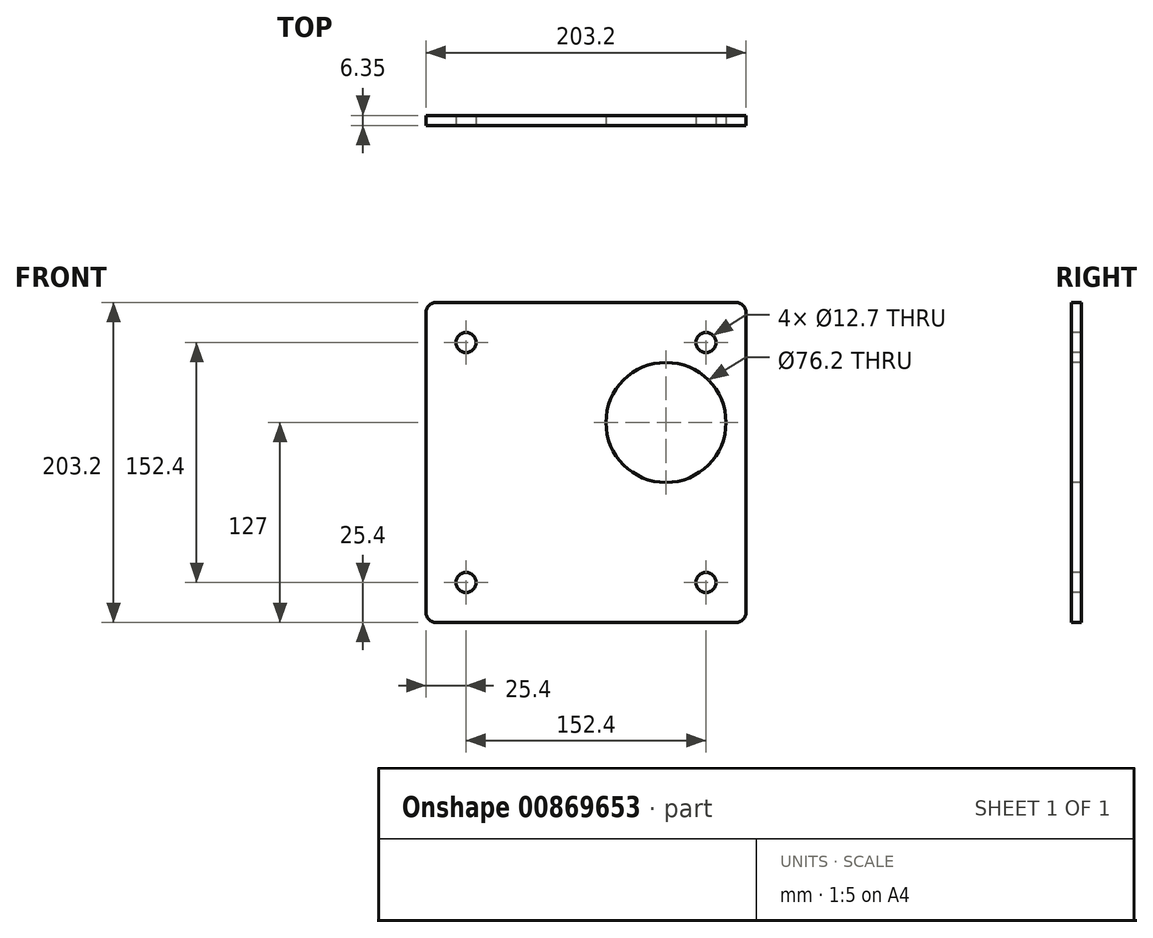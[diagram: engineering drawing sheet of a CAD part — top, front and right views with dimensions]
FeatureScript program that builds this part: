
annotation { "Feature Type Name" : "Feature", "Feature Type Description" : "" }
export const myFeature = defineFeature(function(context is Context, id is Id, definition is map)
    precondition{}
    {
        {
            var Q0;
            Q0=qCreatedBy(makeId("Front.planeOp"),FACE);
            var sketch = newSketch(context, id + "F0", { "sketchPlane" : qUnion([Q0])});
            skLineSegment(sketch, "E0.bottom", {"start": v(101.6, 101.6) * mm, "end": v(-101.6, 101.6) * mm});
            skLineSegment(sketch, "E0.top", {"start": v(101.6, -101.6) * mm, "end": v(-101.6, -101.6) * mm});
            skLineSegment(sketch, "E0.left", {"start": v(101.6, 101.6) * mm, "end": v(101.6, -101.6) * mm});
            skLineSegment(sketch, "E0.right", {"start": v(-101.6, 101.6) * mm, "end": v(-101.6, -101.6) * mm});
            skPoint(sketch, "E0.middle", {"position": v(0, 0) * mm});
            skSolve(sketch);
        }
        {
            var Q0;
            Q0=makeQuery(id+"F0.imprint","IMPRINT",FACE,{"disambiguationData":[TD([[makeQuery(id+"F0.imprint","IMPRINT",EDGE,{"derivedFrom":sQuery(id+"F0.wireOp",EDGE,"E0.bottom")}),1.0]])]});
            extrude(context, id + "F1", {"entities" : qUnion([Q0]), "depth" : 6.35 * mm, "offsetDistance" : 25.4 * mm});
        }
        {
            var Q0;
            Q0=makeQuery(id+"F1.opExtrude","CAP_FACE",FACE,{"disambiguationData":[OSD([sQuery(id+"F0.wireOp",EDGE,"E0.bottom"),sQuery(id+"F0.wireOp",EDGE,"E0.top"),sQuery(id+"F0.wireOp",EDGE,"E0.left"),sQuery(id+"F0.wireOp",EDGE,"E0.right")])],"isStart":false});
            var sketch = newSketch(context, id + "F2", { "sketchPlane" : qUnion([Q0])});
            skCircle(sketch, "E1", {"center": v(-76.2, 76.2) * mm, "radius": 6.35 * mm});
            skCircle(sketch, "E2", {"center": v(76.2, 76.2) * mm, "radius": 6.35 * mm});
            skCircle(sketch, "E3", {"center": v(-76.2, -76.2) * mm, "radius": 6.35 * mm});
            skCircle(sketch, "E4", {"center": v(76.2, -76.2) * mm, "radius": 6.35 * mm});
            skSolve(sketch);
        }
        {
            var Q0;
            Q0 = qSketchRegion(id + "F2", true);
            extrude(context, id + "F3", {"entities" : qUnion([Q0]), "operationType" : NewBodyOperationType.REMOVE, "oppositeDirection" : true, "depth" : 25.4 * mm, "offsetDistance" : 25.4 * mm});
        }
        {
            var Q0;
            Q0=makeQuery(id+"F1.opExtrude","SWEPT_EDGE",EDGE,{"disambiguationData":[OSD([sQuery(id+"F0.wireOp",EDGE,"E0.bottom"),sQuery(id+"F0.wireOp",EDGE,"E0.left")])]});
            var Q1;
            Q1=makeQuery(id+"F1.opExtrude","SWEPT_EDGE",EDGE,{"disambiguationData":[OSD([sQuery(id+"F0.wireOp",EDGE,"E0.bottom"),sQuery(id+"F0.wireOp",EDGE,"E0.right")])]});
            var Q2;
            Q2=makeQuery(id+"F1.opExtrude","SWEPT_EDGE",EDGE,{"disambiguationData":[OSD([sQuery(id+"F0.wireOp",EDGE,"E0.top"),sQuery(id+"F0.wireOp",EDGE,"E0.right")])]});
            var Q3;
            Q3=makeQuery(id+"F1.opExtrude","SWEPT_EDGE",EDGE,{"disambiguationData":[OSD([sQuery(id+"F0.wireOp",EDGE,"E0.top"),sQuery(id+"F0.wireOp",EDGE,"E0.left")])]});
            fillet(context, id + "F4", {"entities" : qUnion([Q0, Q1, Q2, Q3]), "radius" : 6.35 * mm, "tangentPropagation" : true, "allowEdgeOverflow" : false});
        }
        {
            var Q0;
            Q0=makeQuery(id+"F1.opExtrude","CAP_FACE",FACE,{"disambiguationData":[OSD([sQuery(id+"F0.wireOp",EDGE,"E0.bottom"),sQuery(id+"F0.wireOp",EDGE,"E0.top"),sQuery(id+"F0.wireOp",EDGE,"E0.left"),sQuery(id+"F0.wireOp",EDGE,"E0.right")])],"isStart":false});
            var sketch = newSketch(context, id + "F5", { "sketchPlane" : qUnion([Q0])});
            skCircle(sketch, "E5", {"center": v(50.8, 25.4) * mm, "radius": 38.1 * mm});
            skSolve(sketch);
        }
        {
            var Q0;
            Q0=makeQuery(id+"F5.imprint","IMPRINT",FACE,{"disambiguationData":[TD([[makeQuery(id+"F5.imprint","IMPRINT",EDGE,{"derivedFrom":sQuery(id+"F5.wireOp",EDGE,"E5")}),1.0]])]});
            extrude(context, id + "F6", {"entities" : qUnion([Q0]), "operationType" : NewBodyOperationType.REMOVE, "oppositeDirection" : true, "depth" : 25.4 * mm, "offsetDistance" : 25.4 * mm});
        }
    });
